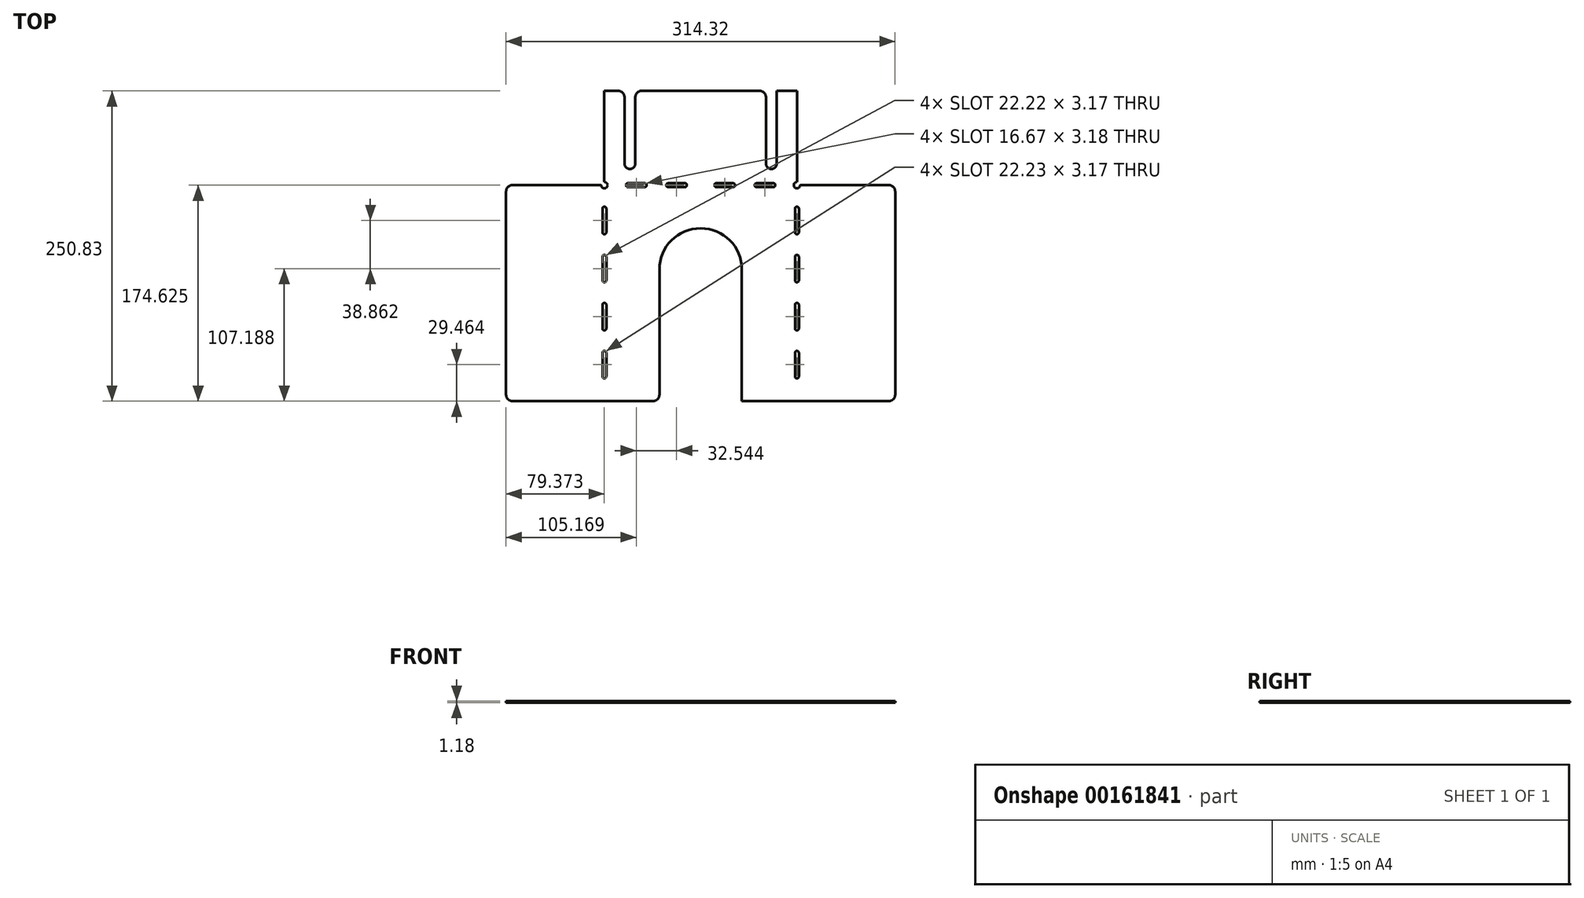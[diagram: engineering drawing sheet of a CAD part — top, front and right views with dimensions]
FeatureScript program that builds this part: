
annotation { "Feature Type Name" : "Feature", "Feature Type Description" : "" }
export const myFeature = defineFeature(function(context is Context, id is Id, definition is map)
    precondition{}
    {
        {
            var Q0;
            Q0=qCreatedBy(makeId("Top.planeOp"),FACE);
            var sketch = newSketch(context, id + "F0", { "sketchPlane" : qUnion([Q0])});
            skLineSegment(sketch, "E0", {"start": v(-77.79, 0) * mm, "end": v(77.79, 0) * mm});
            skLineSegment(sketch, "E1", {"start": v(77.79, 0) * mm, "end": v(77.79, 174.63) * mm});
            skLineSegment(sketch, "E2", {"start": v(77.79, 174.63) * mm, "end": v(-77.79, 174.63) * mm});
            skLineSegment(sketch, "E3", {"start": v(-77.79, 174.63) * mm, "end": v(-77.79, 0) * mm});
            skLineSegment(sketch, "E4", {"start": v(-77.79, 174.63) * mm, "end": v(-157.16, 174.63) * mm});
            skLineSegment(sketch, "E5", {"start": v(-157.16, 174.62) * mm, "end": v(-157.16, 0) * mm});
            skLineSegment(sketch, "E6", {"start": v(-157.16, 0) * mm, "end": v(-77.79, 0) * mm});
            skLineSegment(sketch, "E7", {"start": v(77.79, 174.63) * mm, "end": v(157.16, 174.63) * mm});
            skLineSegment(sketch, "E8", {"start": v(157.16, 174.62) * mm, "end": v(157.16, 0) * mm});
            skLineSegment(sketch, "E9", {"start": v(157.16, 0) * mm, "end": v(77.79, 0) * mm});
            skLineSegment(sketch, "E10", {"start": v(77.79, 174.63) * mm, "end": v(77.79, 250.83) * mm});
            skLineSegment(sketch, "E11", {"start": v(77.79, 250.83) * mm, "end": v(-77.79, 250.83) * mm});
            skLineSegment(sketch, "E12", {"start": v(-77.79, 250.83) * mm, "end": v(-77.79, 174.63) * mm});
            skSolve(sketch);
        }
        {
            var Q0;
            Q0 = qSketchRegion(id + "F0", true);
            extrude(context, id + "F1", {"entities" : qUnion([Q0]), "depth" : 1.18 * mm});
        }
        {
            var Q0;
            Q0=makeQuery(id+"F1.opExtrude","CAP_FACE",FACE,{"disambiguationData":[OSD([sQuery(id+"F0.wireOp",EDGE,"E0"),sQuery(id+"F0.wireOp",EDGE,"E4"),sQuery(id+"F0.wireOp",EDGE,"E5"),sQuery(id+"F0.wireOp",EDGE,"E6"),sQuery(id+"F0.wireOp",EDGE,"E7"),sQuery(id+"F0.wireOp",EDGE,"E8"),sQuery(id+"F0.wireOp",EDGE,"E9"),sQuery(id+"F0.wireOp",EDGE,"E10"),sQuery(id+"F0.wireOp",EDGE,"E11"),sQuery(id+"F0.wireOp",EDGE,"E12")])],"isStart":false});
            var sketch = newSketch(context, id + "F2", { "sketchPlane" : qUnion([Q0])});
            skLineSegment(sketch, "E13", {"start": v(0, -45.26) * mm, "end": v(0, 303.28) * mm, "construction": true});
            skPoint(sketch, "E13.startSnap0", {"position": v(0, 0) * mm});
            skPoint(sketch, "E13.endSnap0", {"position": v(0, 250.83) * mm});
            skArc(sketch, "E14", {"start": v(33.34, 106.36) * mm, "mid": v(0, 139.7) * mm, "end": v(-33.34, 106.36) * mm});
            skLineSegment(sketch, "E15", {"start": v(-33.34, 106.36) * mm, "end": v(-33.34, 0) * mm});
            skLineSegment(sketch, "E16", {"start": v(33.34, 106.36) * mm, "end": v(33.34, 0) * mm});
            skLineSegment(sketch, "E17", {"start": v(-33.34, 0) * mm, "end": v(33.34, 0) * mm});
            skLineSegment(sketch, "E18", {"start": v(57.15, 250.83) * mm, "end": v(57.15, 192.09) * mm, "construction": true});
            skLineSegment(sketch, "E19", {"start": v(-57.15, 250.83) * mm, "end": v(-57.15, 192.09) * mm, "construction": true});
            skArc(sketch, "E20.0.startCap", {"start": v(-61.52, 250.83) * mm, "mid": v(-57.15, 255.2) * mm, "end": v(-52.78, 250.83) * mm});
            skArc(sketch, "E20.0.endCap", {"start": v(-52.78, 192.09) * mm, "mid": v(-57.15, 187.72) * mm, "end": v(-61.52, 192.09) * mm});
            skLineSegment(sketch, "E20.0.left", {"start": v(-52.78, 250.83) * mm, "end": v(-52.78, 192.09) * mm});
            skLineSegment(sketch, "E20.0.right", {"start": v(-61.52, 250.83) * mm, "end": v(-61.52, 192.09) * mm});
            skArc(sketch, "E20.1.startCap", {"start": v(52.78, 250.83) * mm, "mid": v(57.15, 255.2) * mm, "end": v(61.52, 250.83) * mm});
            skArc(sketch, "E20.1.endCap", {"start": v(61.52, 192.09) * mm, "mid": v(57.15, 187.72) * mm, "end": v(52.78, 192.09) * mm});
            skLineSegment(sketch, "E20.1.left", {"start": v(61.52, 250.83) * mm, "end": v(61.52, 192.09) * mm});
            skLineSegment(sketch, "E20.1.right", {"start": v(52.78, 250.83) * mm, "end": v(52.78, 192.09) * mm});
            skSolve(sketch);
        }
        {
            var Q0;
            Q0 = qSketchRegion(id + "F2", true);
            extrude(context, id + "F3", {"entities" : qUnion([Q0]), "operationType" : NewBodyOperationType.REMOVE, "endBound" : BoundingType.UP_TO_NEXT, "oppositeDirection" : true, "depth" : 25.4 * mm});
        }
        {
            var Q0;
            Q0=makeQuery(id+"F1.opExtrude","CAP_FACE",FACE,{"disambiguationData":[OSD([sQuery(id+"F0.wireOp",EDGE,"E0"),sQuery(id+"F0.wireOp",EDGE,"E4"),sQuery(id+"F0.wireOp",EDGE,"E5"),sQuery(id+"F0.wireOp",EDGE,"E6"),sQuery(id+"F0.wireOp",EDGE,"E7"),sQuery(id+"F0.wireOp",EDGE,"E8"),sQuery(id+"F0.wireOp",EDGE,"E9"),sQuery(id+"F0.wireOp",EDGE,"E10"),sQuery(id+"F0.wireOp",EDGE,"E11"),sQuery(id+"F0.wireOp",EDGE,"E12")])],"isStart":false});
            var sketch = newSketch(context, id + "F4", { "sketchPlane" : qUnion([Q0])});
            skLineSegment(sketch, "E21", {"start": v(-77.79, 155.58) * mm, "end": v(-77.79, 136.53) * mm});
            skLineSegment(sketch, "E22", {"start": v(-58.74, 174.63) * mm, "end": v(-45.24, 174.63) * mm});
            skLineSegment(sketch, "E23", {"start": v(0, 0) * mm, "end": v(0, 299.2) * mm, "construction": true});
            skPoint(sketch, "E23.endSnap0", {"position": v(0, 250.83) * mm});
            skPoint(sketch, "E24", {"position": v(-77.79, 155.58) * mm});
            skPoint(sketch, "E25", {"position": v(-77.79, 136.53) * mm});
            skPoint(sketch, "E26.orphan", {"position": v(-77.79, 0) * mm});
            skArc(sketch, "E27.0.startCap", {"start": v(-79.38, 155.58) * mm, "mid": v(-77.79, 157.16) * mm, "end": v(-76.2, 155.58) * mm});
            skArc(sketch, "E27.0.endCap", {"start": v(-76.2, 136.53) * mm, "mid": v(-77.79, 134.94) * mm, "end": v(-79.38, 136.53) * mm});
            skLineSegment(sketch, "E27.0.left", {"start": v(-76.2, 155.58) * mm, "end": v(-76.2, 136.53) * mm});
            skLineSegment(sketch, "E27.0.right", {"start": v(-79.37, 155.58) * mm, "end": v(-79.37, 136.53) * mm});
            skArc(sketch, "E28.0.1.0", {"start": v(-79.38, 116.71) * mm, "mid": v(-77.79, 118.3) * mm, "end": v(-76.2, 116.71) * mm});
            skLineSegment(sketch, "E28.0.1.1", {"start": v(-76.2, 116.71) * mm, "end": v(-76.2, 97.66) * mm});
            skArc(sketch, "E28.0.1.2", {"start": v(-76.2, 97.66) * mm, "mid": v(-77.79, 96.08) * mm, "end": v(-79.38, 97.66) * mm});
            skLineSegment(sketch, "E28.0.1.3", {"start": v(-79.37, 116.71) * mm, "end": v(-79.37, 97.66) * mm});
            skArc(sketch, "E28.0.2.0", {"start": v(-79.38, 77.85) * mm, "mid": v(-77.79, 79.44) * mm, "end": v(-76.2, 77.85) * mm});
            skLineSegment(sketch, "E28.0.2.1", {"start": v(-76.2, 77.85) * mm, "end": v(-76.2, 58.8) * mm});
            skArc(sketch, "E28.0.2.2", {"start": v(-76.2, 58.8) * mm, "mid": v(-77.79, 57.21) * mm, "end": v(-79.38, 58.8) * mm});
            skLineSegment(sketch, "E28.0.2.3", {"start": v(-79.37, 77.85) * mm, "end": v(-79.37, 58.8) * mm});
            skArc(sketch, "E28.0.3.0", {"start": v(-79.38, 38.99) * mm, "mid": v(-77.79, 40.58) * mm, "end": v(-76.2, 38.99) * mm});
            skLineSegment(sketch, "E28.0.3.1", {"start": v(-76.2, 38.99) * mm, "end": v(-76.2, 19.94) * mm});
            skArc(sketch, "E28.0.3.2", {"start": v(-76.2, 19.94) * mm, "mid": v(-77.79, 18.35) * mm, "end": v(-79.38, 19.94) * mm});
            skLineSegment(sketch, "E28.0.3.3", {"start": v(-79.37, 38.99) * mm, "end": v(-79.37, 19.94) * mm});
            skLineSegment(sketch, "E28.direction1", {"start": v(-79.37, 155.58) * mm, "end": v(-53.18, 155.58) * mm, "construction": true});
            skLineSegment(sketch, "E28.direction2", {"start": v(-79.37, 155.58) * mm, "end": v(-79.37, 116.71) * mm, "construction": true});
            skArc(sketch, "E29.MirrorCS", {"start": v(79.38, 155.58) * mm, "mid": v(77.79, 157.16) * mm, "end": v(76.2, 155.58) * mm});
            skArc(sketch, "E30.MirrorCS", {"start": v(76.2, 136.53) * mm, "mid": v(77.79, 134.94) * mm, "end": v(79.38, 136.53) * mm});
            skArc(sketch, "E31.MirrorCS", {"start": v(79.38, 116.71) * mm, "mid": v(77.79, 118.3) * mm, "end": v(76.2, 116.71) * mm});
            skArc(sketch, "E32.MirrorCS", {"start": v(76.2, 58.8) * mm, "mid": v(77.79, 57.21) * mm, "end": v(79.38, 58.8) * mm});
            skArc(sketch, "E33.MirrorCS", {"start": v(79.38, 38.99) * mm, "mid": v(77.79, 40.58) * mm, "end": v(76.2, 38.99) * mm});
            skArc(sketch, "E34.MirrorCS", {"start": v(76.2, 97.66) * mm, "mid": v(77.79, 96.08) * mm, "end": v(79.38, 97.66) * mm});
            skArc(sketch, "E35.MirrorCS", {"start": v(79.38, 77.85) * mm, "mid": v(77.79, 79.44) * mm, "end": v(76.2, 77.85) * mm});
            skArc(sketch, "E36.MirrorCS", {"start": v(76.2, 19.94) * mm, "mid": v(77.79, 18.35) * mm, "end": v(79.38, 19.94) * mm});
            skLineSegment(sketch, "E37.MirrorCS", {"start": v(77.79, 155.58) * mm, "end": v(77.79, 136.53) * mm});
            skLineSegment(sketch, "E38.MirrorCS", {"start": v(79.37, 155.58) * mm, "end": v(79.38, 136.53) * mm});
            skLineSegment(sketch, "E39.MirrorCS", {"start": v(79.37, 155.58) * mm, "end": v(79.37, 116.71) * mm, "construction": true});
            skLineSegment(sketch, "E40.MirrorCS", {"start": v(79.37, 155.58) * mm, "end": v(53.18, 155.58) * mm, "construction": true});
            skLineSegment(sketch, "E41.MirrorCS", {"start": v(79.38, 77.85) * mm, "end": v(79.38, 58.8) * mm});
            skLineSegment(sketch, "E42.MirrorCS", {"start": v(76.2, 38.99) * mm, "end": v(76.2, 19.94) * mm});
            skLineSegment(sketch, "E43.MirrorCS", {"start": v(76.2, 155.58) * mm, "end": v(76.2, 136.53) * mm});
            skLineSegment(sketch, "E44.MirrorCS", {"start": v(76.2, 116.71) * mm, "end": v(76.2, 97.66) * mm});
            skLineSegment(sketch, "E45.MirrorCS", {"start": v(79.37, 116.71) * mm, "end": v(79.38, 97.66) * mm});
            skLineSegment(sketch, "E46.MirrorCS", {"start": v(79.38, 38.99) * mm, "end": v(79.38, 19.94) * mm});
            skLineSegment(sketch, "E47.MirrorCS", {"start": v(76.2, 77.85) * mm, "end": v(76.2, 58.8) * mm});
            skPoint(sketch, "E48", {"position": v(0, 174.63) * mm});
            skPoint(sketch, "E49", {"position": v(-12.7, 174.63) * mm});
            skPoint(sketch, "E50", {"position": v(12.7, 174.63) * mm});
            skPoint(sketch, "E51", {"position": v(-58.74, 174.63) * mm});
            skPoint(sketch, "E52", {"position": v(-26.2, 174.63) * mm});
            skPoint(sketch, "E53", {"position": v(45.24, 174.63) * mm});
            skPoint(sketch, "E54", {"position": v(58.74, 174.63) * mm});
            skPoint(sketch, "E55.orphan", {"position": v(-77.79, 174.63) * mm});
            skPoint(sketch, "E56.orphan", {"position": v(77.79, 174.63) * mm});
            skLineSegment(sketch, "E57.trimOffspring", {"start": v(12.7, 174.63) * mm, "end": v(26.2, 174.63) * mm});
            skPoint(sketch, "E58", {"position": v(-45.24, 174.63) * mm});
            skPoint(sketch, "E59", {"position": v(26.2, 174.63) * mm});
            skLineSegment(sketch, "E60.trimOffspring", {"start": v(-26.2, 174.63) * mm, "end": v(-12.7, 174.63) * mm});
            skLineSegment(sketch, "E61.trimOffspring", {"start": v(45.24, 174.63) * mm, "end": v(58.74, 174.63) * mm});
            skArc(sketch, "E62.0.startCap", {"start": v(-58.74, 173.04) * mm, "mid": v(-60.33, 174.63) * mm, "end": v(-58.74, 176.21) * mm});
            skArc(sketch, "E62.0.endCap", {"start": v(-45.24, 176.21) * mm, "mid": v(-43.66, 174.63) * mm, "end": v(-45.24, 173.04) * mm});
            skLineSegment(sketch, "E62.0.left", {"start": v(-58.74, 176.21) * mm, "end": v(-45.24, 176.21) * mm});
            skLineSegment(sketch, "E62.0.right", {"start": v(-58.74, 173.04) * mm, "end": v(-45.24, 173.04) * mm});
            skArc(sketch, "E62.1.startCap", {"start": v(-26.2, 173.04) * mm, "mid": v(-27.78, 174.63) * mm, "end": v(-26.2, 176.21) * mm});
            skArc(sketch, "E62.1.endCap", {"start": v(-12.7, 176.21) * mm, "mid": v(-11.11, 174.63) * mm, "end": v(-12.7, 173.04) * mm});
            skLineSegment(sketch, "E62.1.left", {"start": v(-26.2, 176.21) * mm, "end": v(-12.7, 176.21) * mm});
            skLineSegment(sketch, "E62.1.right", {"start": v(-26.2, 173.04) * mm, "end": v(-12.7, 173.04) * mm});
            skArc(sketch, "E62.2.startCap", {"start": v(12.7, 173.04) * mm, "mid": v(11.11, 174.63) * mm, "end": v(12.7, 176.21) * mm});
            skArc(sketch, "E62.2.endCap", {"start": v(26.2, 176.21) * mm, "mid": v(27.78, 174.63) * mm, "end": v(26.2, 173.04) * mm});
            skLineSegment(sketch, "E62.2.left", {"start": v(12.7, 176.21) * mm, "end": v(26.2, 176.21) * mm});
            skLineSegment(sketch, "E62.2.right", {"start": v(12.7, 173.04) * mm, "end": v(26.2, 173.04) * mm});
            skArc(sketch, "E62.3.startCap", {"start": v(45.24, 173.04) * mm, "mid": v(43.66, 174.63) * mm, "end": v(45.24, 176.21) * mm});
            skArc(sketch, "E62.3.endCap", {"start": v(58.74, 176.21) * mm, "mid": v(60.33, 174.63) * mm, "end": v(58.74, 173.04) * mm});
            skLineSegment(sketch, "E62.3.left", {"start": v(45.24, 176.21) * mm, "end": v(58.74, 176.21) * mm});
            skLineSegment(sketch, "E62.3.right", {"start": v(45.24, 173.04) * mm, "end": v(58.74, 173.04) * mm});
            skCircle(sketch, "E63", {"center": v(-77.79, 174.63) * mm, "radius": 2.54 * mm});
            skCircle(sketch, "E64", {"center": v(77.79, 174.63) * mm, "radius": 2.54 * mm});
            skSolve(sketch);
        }
        {
            var Q0;
            Q0 = qSketchRegion(id + "F4", true);
            var Q1;
            Q1=makeQuery(id+"F1.opExtrude","SWEPT_BODY",BODY,{"disambiguationData":[OSD([sQuery(id+"F0.wireOp",EDGE,"E0"),sQuery(id+"F0.wireOp",EDGE,"E4"),sQuery(id+"F0.wireOp",EDGE,"E5"),sQuery(id+"F0.wireOp",EDGE,"E6"),sQuery(id+"F0.wireOp",EDGE,"E7"),sQuery(id+"F0.wireOp",EDGE,"E8"),sQuery(id+"F0.wireOp",EDGE,"E9"),sQuery(id+"F0.wireOp",EDGE,"E10"),sQuery(id+"F0.wireOp",EDGE,"E11"),sQuery(id+"F0.wireOp",EDGE,"E12")])]});
            extrude(context, id + "F5", {"entities" : qUnion([Q0]), "operationType" : NewBodyOperationType.REMOVE, "endBound" : BoundingType.UP_TO_NEXT, "oppositeDirection" : true, "endBoundEntityBody" : qUnion([Q1]), "depth" : 25.4 * mm});
        }
        {
            var Q0;
            Q0=makeQuery(id+"F1.opExtrude","SWEPT_EDGE",EDGE,{"disambiguationData":[OSD([sQuery(id+"F0.wireOp",EDGE,"E4"),sQuery(id+"F0.wireOp",EDGE,"E5")])]});
            var Q1;
            Q1=makeQuery(id+"F3.boolean.opBoolean","COPY",EDGE,{"derivedFrom":makeQuery(id+"F3.opExtrude","TWEAK_EDGE",EDGE,{"derivedFrom":[makeQuery(id+"F1.opExtrude","SWEPT_FACE",FACE,{"disambiguationData":[OSD([sQuery(id+"F0.wireOp",EDGE,"E11")])]}),makeQuery(id+"F2.imprint","IMPRINT",EDGE,{"derivedFrom":sQuery(id+"F2.wireOp",EDGE,"E20.0.right")})]})});
            var Q2;
            Q2=makeQuery(id+"F3.boolean.opBoolean","COPY",EDGE,{"derivedFrom":makeQuery(id+"F3.opExtrude","TWEAK_EDGE",EDGE,{"derivedFrom":[makeQuery(id+"F1.opExtrude","SWEPT_FACE",FACE,{"disambiguationData":[OSD([sQuery(id+"F0.wireOp",EDGE,"E11")])]}),makeQuery(id+"F2.imprint","IMPRINT",EDGE,{"derivedFrom":sQuery(id+"F2.wireOp",EDGE,"E20.0.left")})]})});
            var Q3;
            Q3=makeQuery(id+"F3.boolean.opBoolean","COPY",EDGE,{"derivedFrom":makeQuery(id+"F3.opExtrude","TWEAK_EDGE",EDGE,{"derivedFrom":[makeQuery(id+"F1.opExtrude","SWEPT_FACE",FACE,{"disambiguationData":[OSD([sQuery(id+"F0.wireOp",EDGE,"E11")])]}),makeQuery(id+"F2.imprint","IMPRINT",EDGE,{"derivedFrom":sQuery(id+"F2.wireOp",EDGE,"E20.1.right")})]})});
            var Q4;
            Q4=makeQuery(id+"F3.boolean.opBoolean","COPY",EDGE,{"derivedFrom":makeQuery(id+"F3.opExtrude","TWEAK_EDGE",EDGE,{"derivedFrom":[makeQuery(id+"F1.opExtrude","SWEPT_FACE",FACE,{"disambiguationData":[OSD([sQuery(id+"F0.wireOp",EDGE,"E11")])]}),makeQuery(id+"F2.imprint","IMPRINT",EDGE,{"derivedFrom":sQuery(id+"F2.wireOp",EDGE,"E20.1.left")})]})});
            var Q5;
            Q5=makeQuery(id+"F1.opExtrude","SWEPT_EDGE",EDGE,{"disambiguationData":[OSD([sQuery(id+"F0.wireOp",EDGE,"E7"),sQuery(id+"F0.wireOp",EDGE,"E8")])]});
            var Q6;
            Q6=makeQuery(id+"F1.opExtrude","SWEPT_EDGE",EDGE,{"disambiguationData":[OSD([sQuery(id+"F0.wireOp",EDGE,"E5"),sQuery(id+"F0.wireOp",EDGE,"E6")])]});
            var Q7;
            Q7=makeQuery(id+"F3.boolean.opBoolean","COPY",EDGE,{"derivedFrom":makeQuery(id+"F3.opExtrude","SWEPT_EDGE",EDGE,{"disambiguationData":[OSD([sQuery(id+"F0.wireOp",EDGE,"E0"),sQuery(id+"F0.wireOp",EDGE,"E6"),sQuery(id+"F0.wireOp",EDGE,"E9"),sQuery(id+"F2.wireOp",EDGE,"E16"),sQuery(id+"F2.wireOp",EDGE,"E17")])]})});
            var Q8;
            Q8=makeQuery(id+"F3.boolean.opBoolean","COPY",EDGE,{"derivedFrom":makeQuery(id+"F3.opExtrude","SWEPT_EDGE",EDGE,{"disambiguationData":[OSD([sQuery(id+"F0.wireOp",EDGE,"E0"),sQuery(id+"F0.wireOp",EDGE,"E6"),sQuery(id+"F0.wireOp",EDGE,"E9"),sQuery(id+"F2.wireOp",EDGE,"E15"),sQuery(id+"F2.wireOp",EDGE,"E17")])]})});
            var Q9;
            Q9=makeQuery(id+"F1.opExtrude","SWEPT_EDGE",EDGE,{"disambiguationData":[OSD([sQuery(id+"F0.wireOp",EDGE,"E8"),sQuery(id+"F0.wireOp",EDGE,"E9")])]});
            fillet(context, id + "F6", {"entities" : qUnion([Q0, Q1, Q2, Q3, Q4, Q5, Q6, Q7, Q8, Q9]), "radius" : 5.08 * mm, "tangentPropagation" : true, "allowEdgeOverflow" : false});
        }
    });
